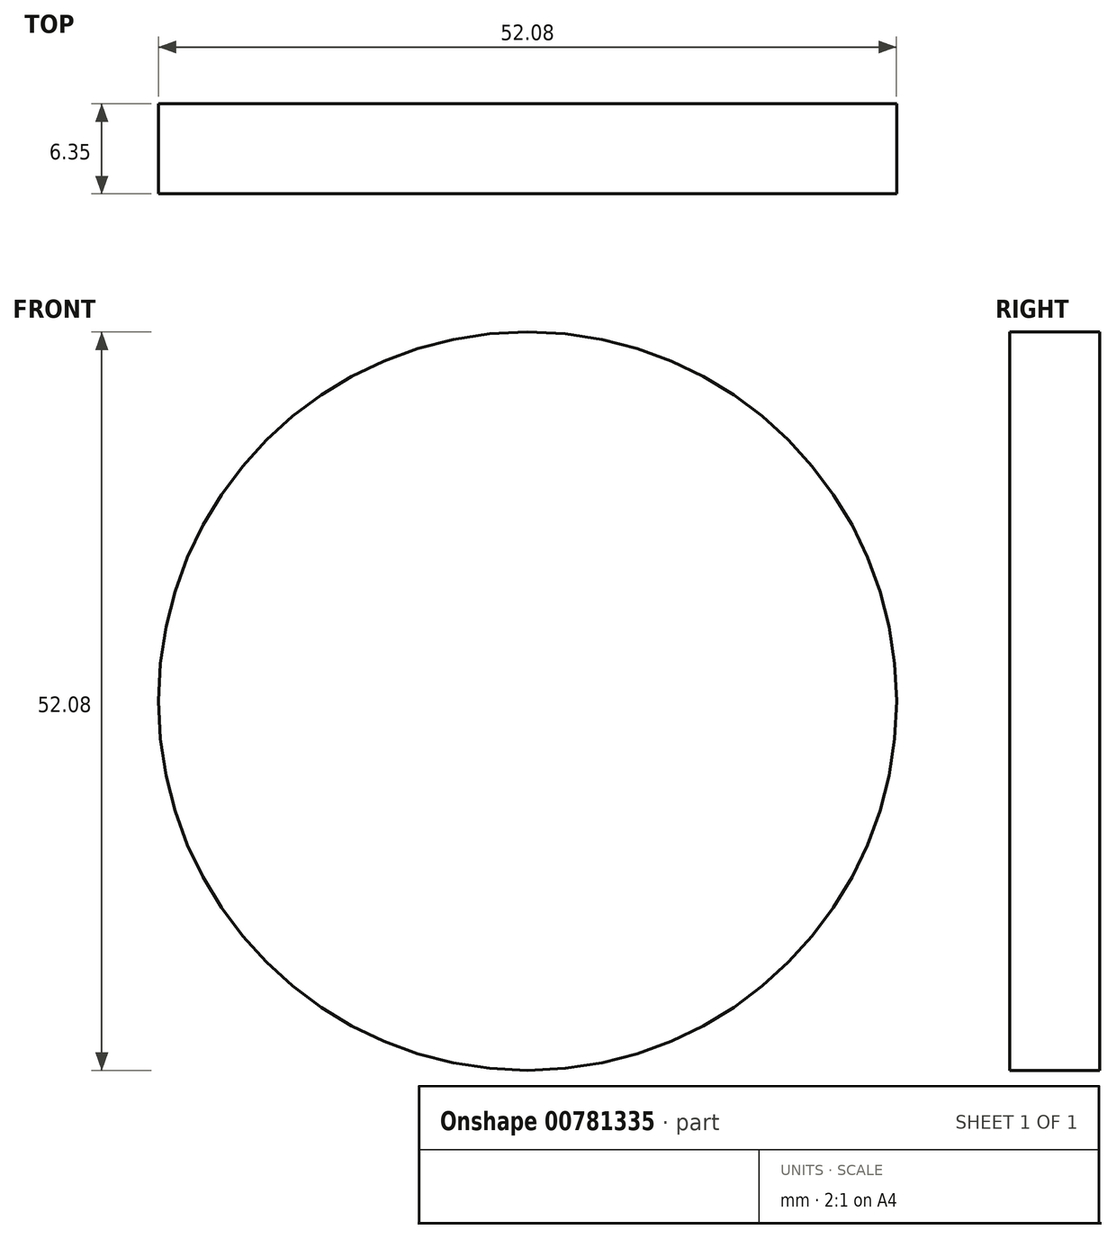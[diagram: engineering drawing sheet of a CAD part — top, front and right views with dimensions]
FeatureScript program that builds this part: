
annotation { "Feature Type Name" : "Feature", "Feature Type Description" : "" }
export const myFeature = defineFeature(function(context is Context, id is Id, definition is map)
    precondition{}
    {
        {
            var Q0;
            Q0=qCreatedBy(makeId("Front.planeOp"),FACE);
            var sketch = newSketch(context, id + "F0", { "sketchPlane" : qUnion([Q0])});
            skCircle(sketch, "E0", {"center": v(0, 0) * mm, "radius": 26.04 * mm});
            skSolve(sketch);
        }
        {
            var Q0;
            Q0=makeQuery(id+"F0.imprint","IMPRINT",FACE,{"disambiguationData":[TD([[makeQuery(id+"F0.imprint","IMPRINT",EDGE,{"derivedFrom":sQuery(id+"F0.wireOp",EDGE,"E0")}),1.0]])]});
            extrude(context, id + "F1", {"entities" : qUnion([Q0]), "depth" : 6.35 * mm, "offsetDistance" : 25.4 * mm});
        }
    });
